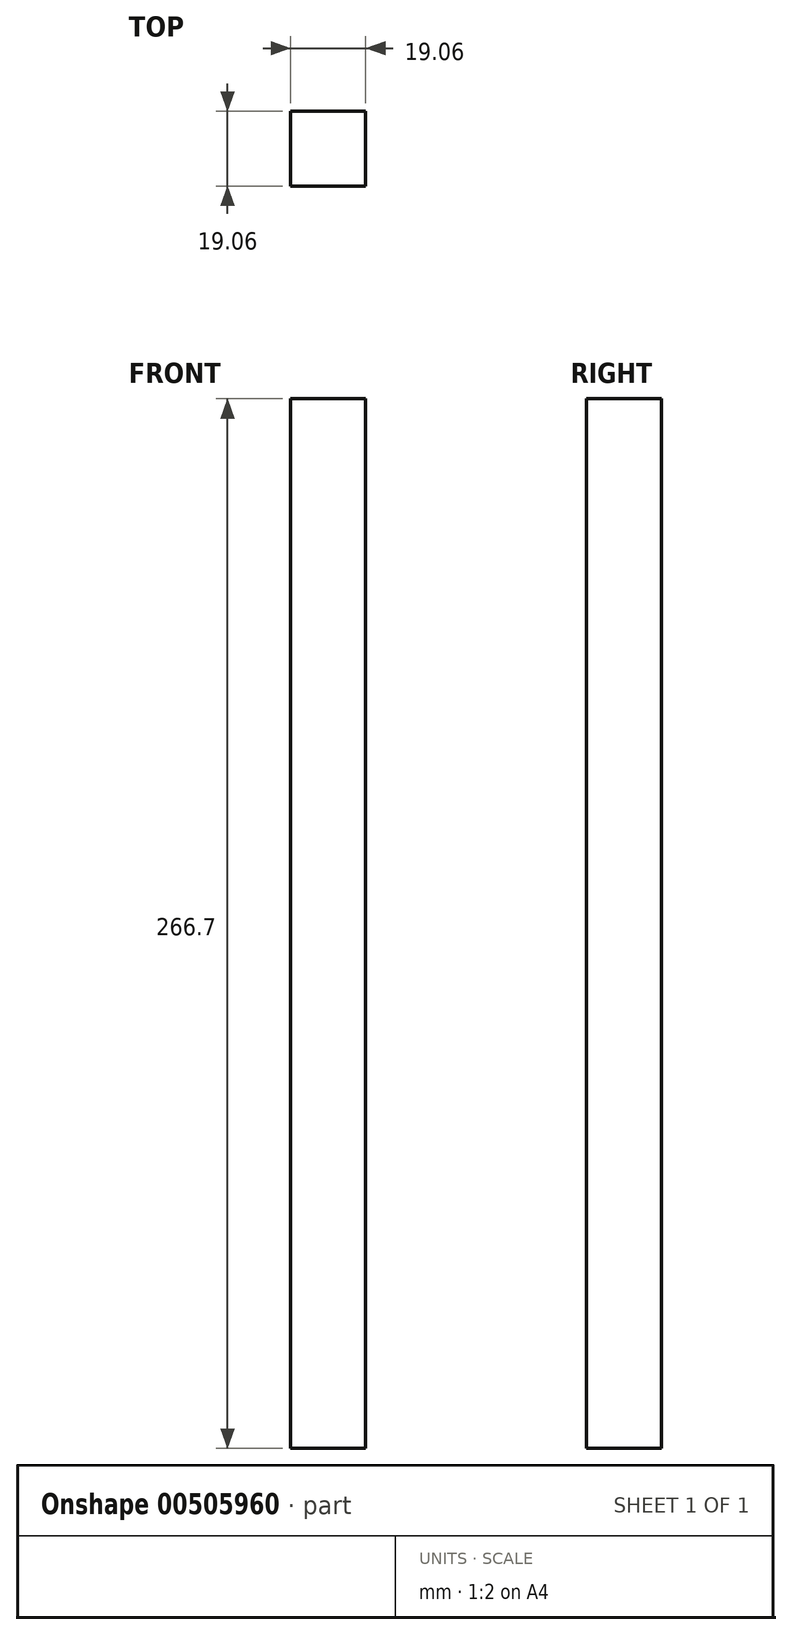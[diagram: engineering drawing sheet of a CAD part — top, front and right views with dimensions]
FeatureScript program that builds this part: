
annotation { "Feature Type Name" : "Feature", "Feature Type Description" : "" }
export const myFeature = defineFeature(function(context is Context, id is Id, definition is map)
    precondition{}
    {
        {
            var Q0;
            Q0=qCreatedBy(makeId("Top.planeOp"),FACE);
            var sketch = newSketch(context, id + "F0", { "sketchPlane" : qUnion([Q0])});
            skLineSegment(sketch, "E0.bottom", {"start": v(-9.52, 9.52) * mm, "end": v(9.53, 9.52) * mm});
            skLineSegment(sketch, "E0.top", {"start": v(-9.53, -9.53) * mm, "end": v(9.52, -9.53) * mm});
            skLineSegment(sketch, "E0.left", {"start": v(-9.52, 9.52) * mm, "end": v(-9.53, -9.53) * mm});
            skLineSegment(sketch, "E0.right", {"start": v(9.53, 9.52) * mm, "end": v(9.52, -9.53) * mm});
            skPoint(sketch, "E0.middle", {"position": v(0, 0) * mm});
            skSolve(sketch);
        }
        {
            var Q0;
            Q0=qSketchRegion(id+"F0",true);
            extrude(context, id + "F1", {"entities" : qUnion([Q0]), "depth" : 266.7 * mm, "offsetDistance" : 25.4 * mm});
        }
    });
